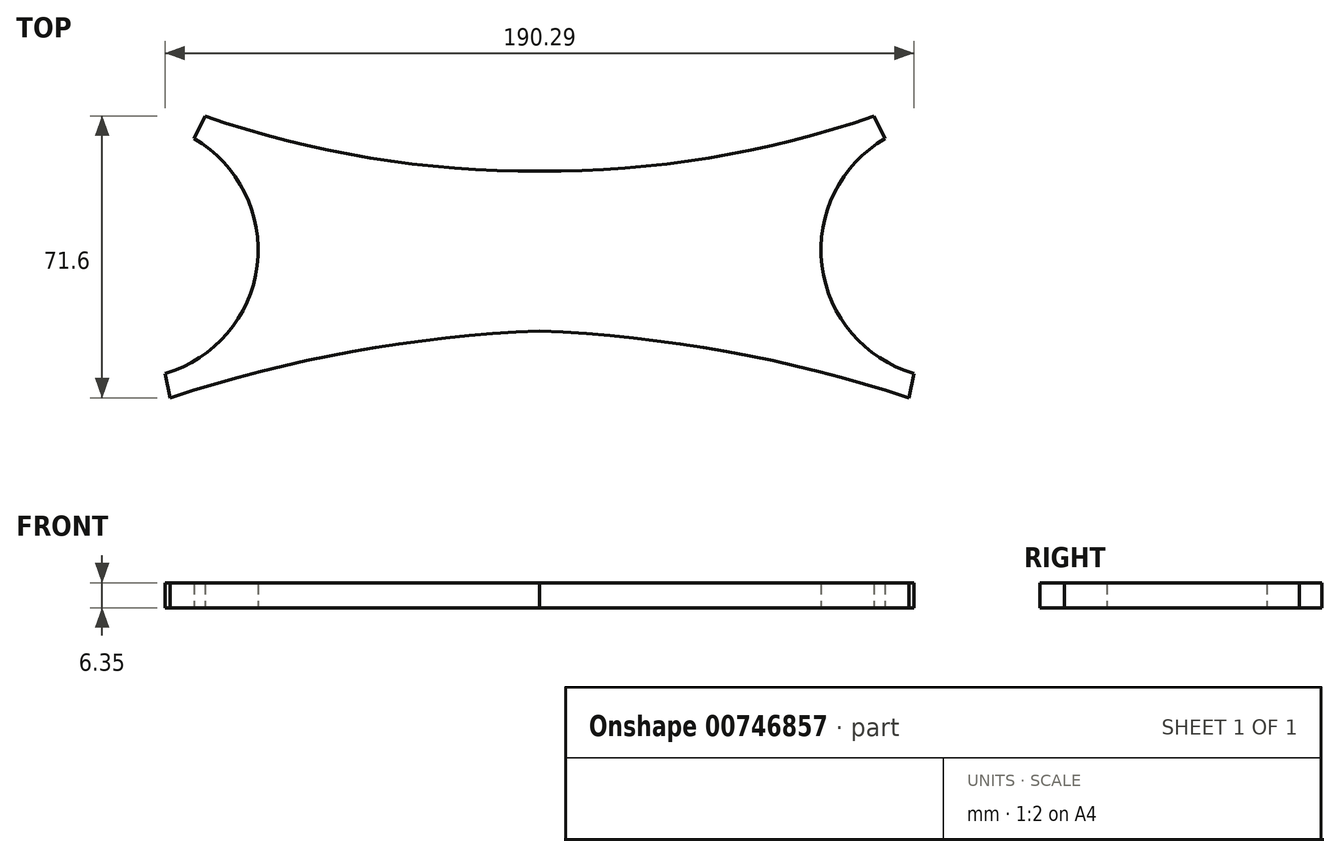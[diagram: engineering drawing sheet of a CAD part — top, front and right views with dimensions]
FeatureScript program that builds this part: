
annotation { "Feature Type Name" : "Feature", "Feature Type Description" : "" }
export const myFeature = defineFeature(function(context is Context, id is Id, definition is map)
    precondition{}
    {
        {
            var Q0;
            Q0=qCreatedBy(makeId("Top.planeOp"),FACE);
            var sketch = newSketch(context, id + "F0", { "sketchPlane" : qUnion([Q0])});
            skLineSegment(sketch, "E0", {"start": v(150.45, -46.98) * mm, "end": v(151.74, -40.76) * mm});
            skLineSegment(sketch, "E1", {"start": v(141.6, 24.62) * mm, "end": v(144.36, 18.9) * mm});
            skArc(sketch, "E2", {"start": v(150.45, -46.98) * mm, "mid": v(104.11, -35.22) * mm, "end": v(56.6, -30) * mm});
            skLineSegment(sketch, "E3.MirrorCS", {"start": v(-37.26, -46.98) * mm, "end": v(-38.55, -40.76) * mm});
            skLineSegment(sketch, "E4.MirrorCS", {"start": v(-28.4, 24.62) * mm, "end": v(-31.17, 18.9) * mm});
            skArc(sketch, "E5.MirrorCS", {"start": v(-37.26, -46.98) * mm, "mid": v(9.08, -35.22) * mm, "end": v(56.6, -30) * mm});
            skArc(sketch, "E6", {"start": v(56.6, 10.65) * mm, "mid": v(99.7, 14) * mm, "end": v(141.6, 24.62) * mm});
            skArc(sketch, "E7.MirrorCS", {"start": v(56.6, 10.65) * mm, "mid": v(13.5, 14) * mm, "end": v(-28.4, 24.62) * mm});
            skArc(sketch, "E8", {"start": v(-38.55, -40.76) * mm, "mid": v(-15.16, -13.37) * mm, "end": v(-31.17, 18.9) * mm});
            skArc(sketch, "E9.MirrorCS", {"start": v(151.74, -40.76) * mm, "mid": v(128.35, -13.37) * mm, "end": v(144.36, 18.9) * mm});
            skSolve(sketch);
        }
        {
            var Q0;
            Q0=makeQuery(id+"F0.imprint","IMPRINT",FACE,{"disambiguationData":[TD([[makeQuery(id+"F0.imprint","IMPRINT",EDGE,{"derivedFrom":sQuery(id+"F0.wireOp",EDGE,"E0")}),1.0]])]});
            extrude(context, id + "F1", {"entities" : qUnion([Q0]), "depth" : 6.35 * mm, "offsetDistance" : 25.4 * mm});
        }
    });
